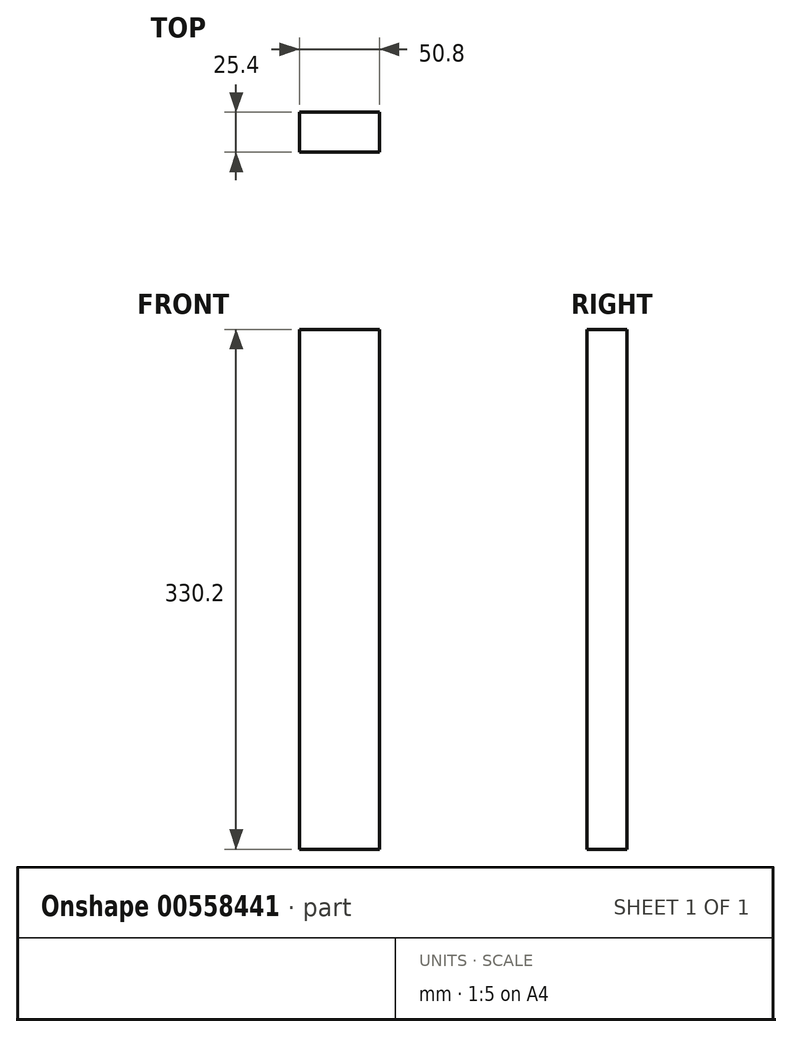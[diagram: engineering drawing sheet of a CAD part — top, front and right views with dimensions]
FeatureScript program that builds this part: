
annotation { "Feature Type Name" : "Feature", "Feature Type Description" : "" }
export const myFeature = defineFeature(function(context is Context, id is Id, definition is map)
    precondition{}
    {
        {
            var Q0;
            Q0=qCreatedBy(makeId("Front.planeOp"),FACE);
            var sketch = newSketch(context, id + "F0", { "sketchPlane" : qUnion([Q0])});
            skLineSegment(sketch, "E0", {"start": v(-67.03, 396.72) * mm, "end": v(-67.03, 66.52) * mm});
            skLineSegment(sketch, "E1", {"start": v(-67.03, 396.72) * mm, "end": v(-16.23, 396.72) * mm});
            skLineSegment(sketch, "E2", {"start": v(-16.23, 396.72) * mm, "end": v(-16.23, 66.52) * mm});
            skLineSegment(sketch, "E3", {"start": v(-16.23, 66.52) * mm, "end": v(-67.03, 66.52) * mm});
            skSolve(sketch);
        }
        {
            var Q0;
            Q0 = qSketchRegion(id + "F0", true);
            extrude(context, id + "F1", {"entities" : qUnion([Q0]), "depth" : 25.4 * mm, "offsetDistance" : 25.4 * mm});
        }
    });
